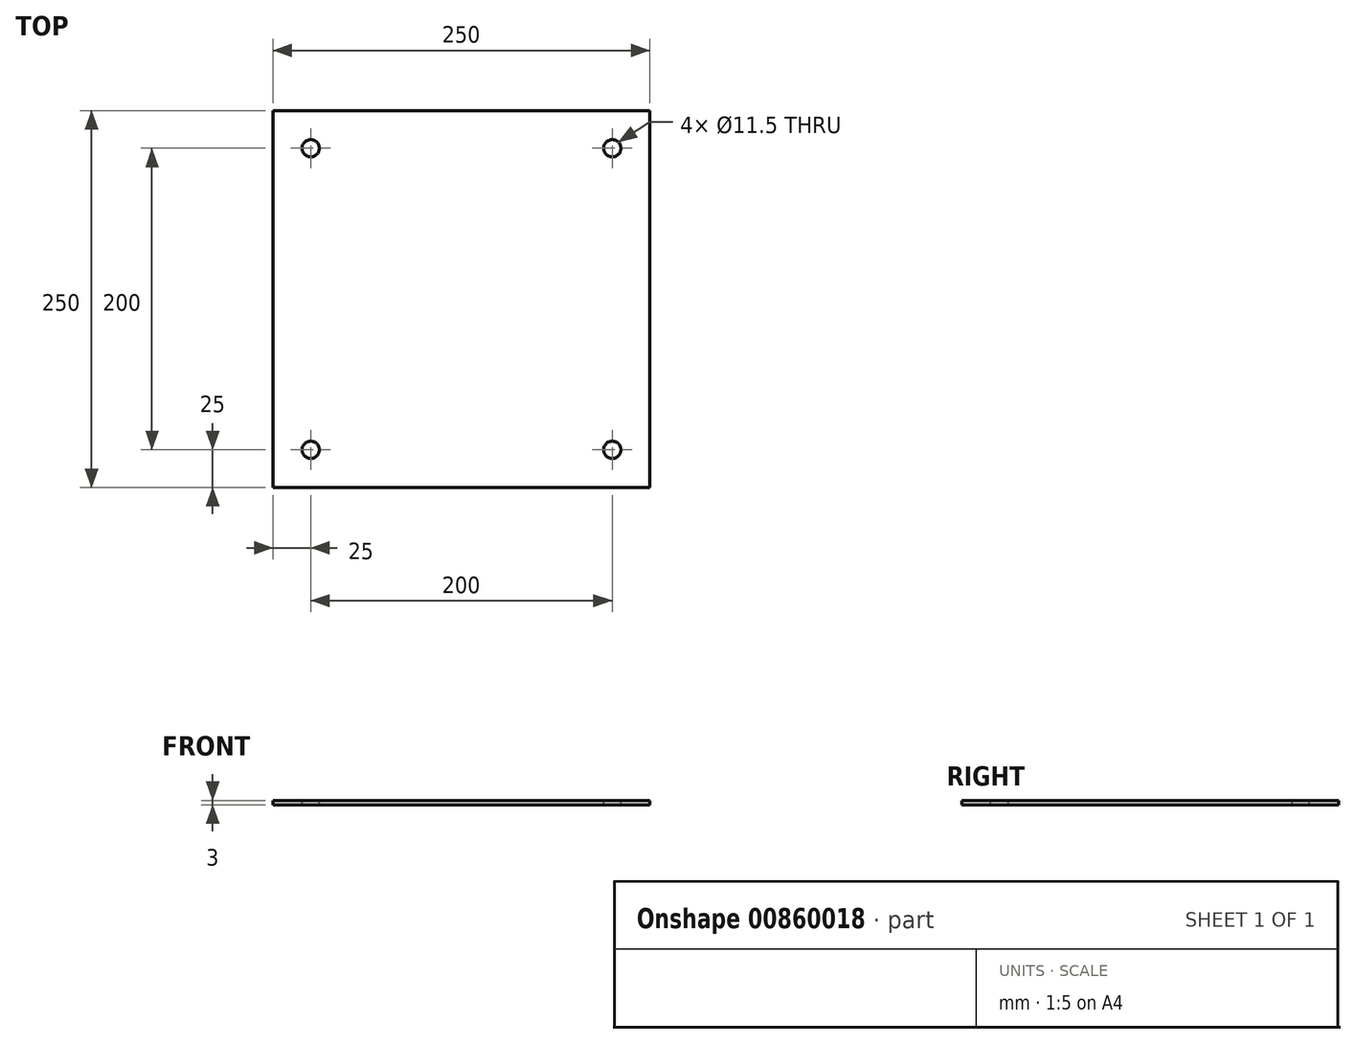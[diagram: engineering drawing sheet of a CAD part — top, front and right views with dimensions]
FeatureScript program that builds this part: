
annotation { "Feature Type Name" : "Feature", "Feature Type Description" : "" }
export const myFeature = defineFeature(function(context is Context, id is Id, definition is map)
    precondition{}
    {
        {
            var Q0;
            Q0=qCreatedBy(makeId("Top.planeOp"),FACE);
            var sketch = newSketch(context, id + "F0", { "sketchPlane" : qUnion([Q0])});
            skLineSegment(sketch, "E0.bottom", {"start": v(125, 125) * mm, "end": v(-125, 125) * mm});
            skLineSegment(sketch, "E0.top", {"start": v(125, -125) * mm, "end": v(-125, -125) * mm});
            skLineSegment(sketch, "E0.left", {"start": v(125, 125) * mm, "end": v(125, -125) * mm});
            skLineSegment(sketch, "E0.right", {"start": v(-125, 125) * mm, "end": v(-125, -125) * mm});
            skPoint(sketch, "E0.middle", {"position": v(0, 0) * mm});
            skSolve(sketch);
        }
        {
            var Q0;
            Q0=makeQuery(id+"F0.imprint","IMPRINT",FACE,{"disambiguationData":[TD([[makeQuery(id+"F0.imprint","IMPRINT",EDGE,{"derivedFrom":sQuery(id+"F0.wireOp",EDGE,"E0.bottom")}),1.0]])]});
            extrude(context, id + "F1", {"entities" : qUnion([Q0]), "depth" : 3 * mm, "offsetDistance" : 25 * mm});
        }
        {
            var Q0;
            Q0=makeQuery(id+"F1.opExtrude","CAP_FACE",FACE,{"disambiguationData":[OSD([sQuery(id+"F0.wireOp",EDGE,"E0.bottom"),sQuery(id+"F0.wireOp",EDGE,"E0.top"),sQuery(id+"F0.wireOp",EDGE,"E0.left"),sQuery(id+"F0.wireOp",EDGE,"E0.right")])],"isStart":false});
            var sketch = newSketch(context, id + "F2", { "sketchPlane" : qUnion([Q0])});
            skLineSegment(sketch, "E1.bottom", {"start": v(100, 100) * mm, "end": v(-100, 100) * mm, "construction": true});
            skLineSegment(sketch, "E1.top", {"start": v(100, -100) * mm, "end": v(-100, -100) * mm, "construction": true});
            skLineSegment(sketch, "E1.left", {"start": v(100, 100) * mm, "end": v(100, -100) * mm, "construction": true});
            skLineSegment(sketch, "E1.right", {"start": v(-100, 100) * mm, "end": v(-100, -100) * mm, "construction": true});
            skPoint(sketch, "E1.middle", {"position": v(0, 0) * mm});
            skSolve(sketch);
        }
        {
            var Q0;
            Q0=sQuery(id+"F2.wireOp",VERTEX,"E1.bottom.end");
            var Q1;
            Q1=sQuery(id+"F2.wireOp",VERTEX,"E1.bottom.start");
            var Q2;
            Q2=sQuery(id+"F2.wireOp",VERTEX,"E1.top.start");
            var Q3;
            Q3=sQuery(id+"F2.wireOp",VERTEX,"E1.top.end");
            var Q4;
            Q4=makeQuery(id+"F1.opExtrude","SWEPT_BODY",BODY,{"disambiguationData":[OSD([sQuery(id+"F0.wireOp",EDGE,"E0.bottom"),sQuery(id+"F0.wireOp",EDGE,"E0.top"),sQuery(id+"F0.wireOp",EDGE,"E0.left"),sQuery(id+"F0.wireOp",EDGE,"E0.right")])]});
            hole(context, id + "F3", {"style" : HoleStyle.SIMPLE, "endStyle" : HoleEndStyle.THROUGH, "holeDiameter" : 11.5 * mm, "majorDiameter" : 5 * mm, "isTappedThrough" : true, "tappedDepth" : 12 * mm, "tapClearance" : 3, "locations" : qUnion([Q0, Q1, Q2, Q3]), "scope" : qUnion([Q4])});
        }
    });
